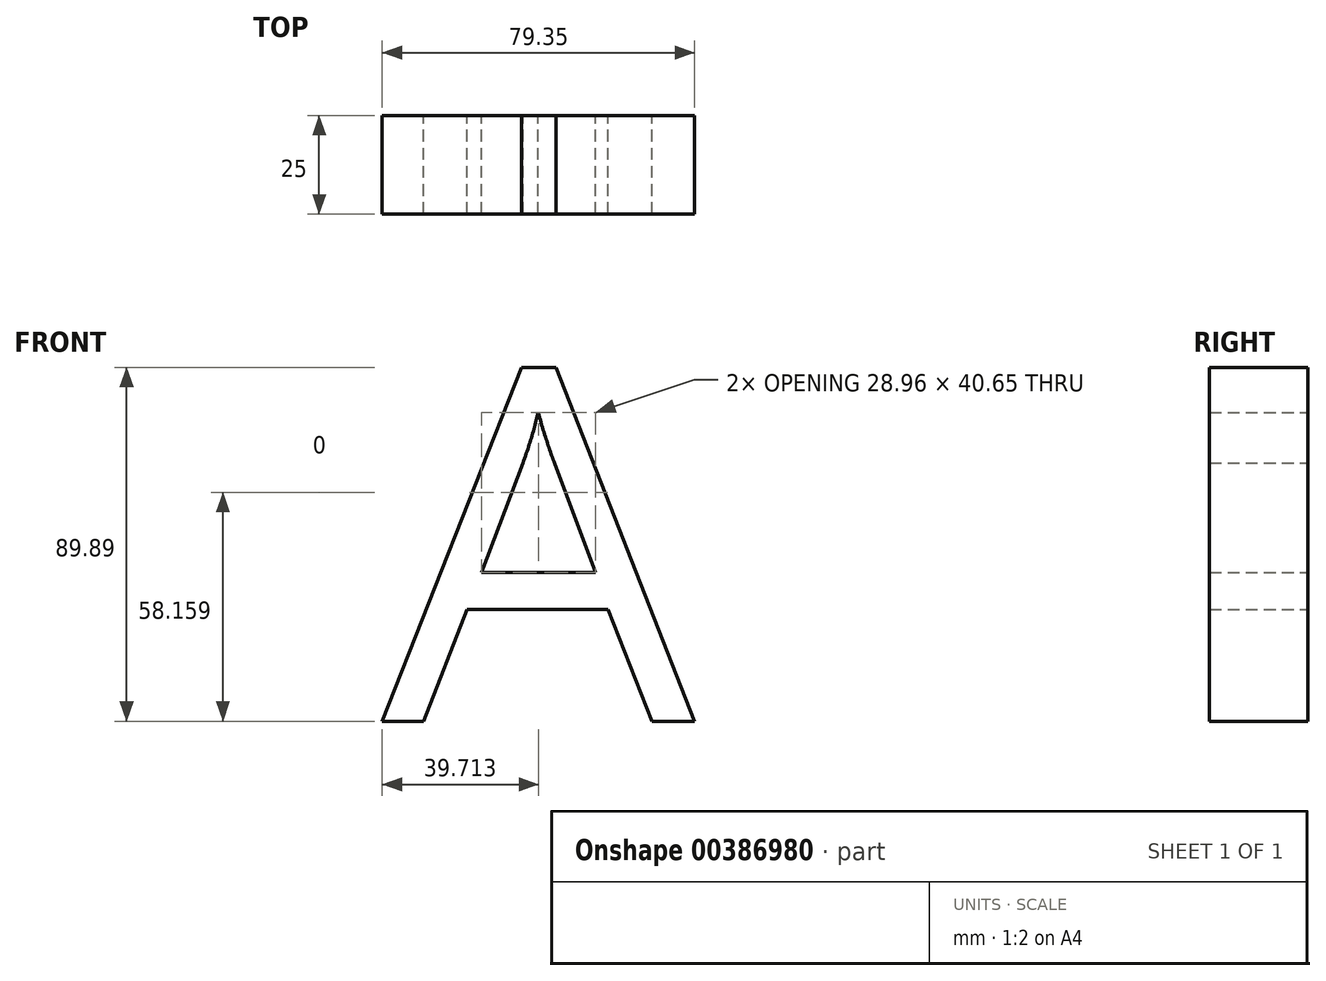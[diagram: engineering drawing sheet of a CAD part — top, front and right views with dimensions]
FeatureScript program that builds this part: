
annotation { "Feature Type Name" : "Feature", "Feature Type Description" : "" }
export const myFeature = defineFeature(function(context is Context, id is Id, definition is map)
    precondition{}
    {
        {
            var Q0;
            Q0=qCreatedBy(makeId("Front.planeOp"),FACE);
            var sketch = newSketch(context, id + "F0", { "sketchPlane" : qUnion([Q0])});
            skText(sketch, "E0", { "text": "A", "fontName": "OpenSans-Regular.ttf"});
            const initialGuessF0  = {"E0": [-0.04893, -0.04248, 1, 0, 0.09028]};
            skSetInitialGuess(sketch, initialGuessF0);
            skSolve(sketch);
        }
        {
            var Q0;
            Q0 = qSketchRegion(id + "F0", true);
            extrude(context, id + "F1", {"entities" : qUnion([Q0]), "depth" : 25 * mm});
        }
    });
